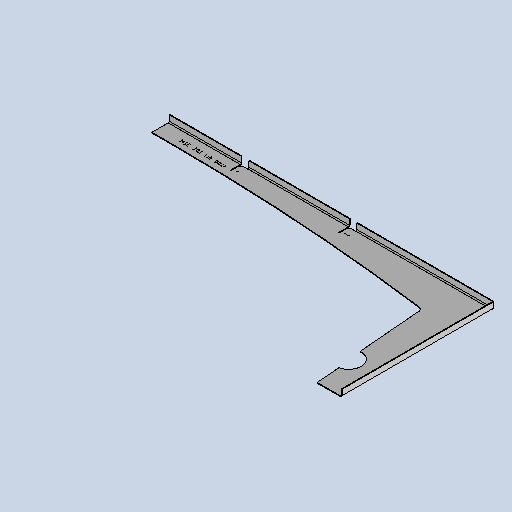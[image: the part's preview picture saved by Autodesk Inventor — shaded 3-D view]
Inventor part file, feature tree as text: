
AUTODESK INVENTOR PART (.ipt)
format: ipt  version: 2025 (Build 290162010, 162A)  size: 378,880 bytes
history: native  units: mm
features: other x6, sheet_metal_op x4, sketch x4, extrude x1
ambient origin geometry x8: Origin, YZ Plane, XZ Plane, XY Plane, X Axis, Y Axis, Z Axis, Center Point
bodies: Solid1 (feature_tree)
feature tree (15):
  sheet_metal_op  "Face1"
  other  "Mark3"
  sheet_metal_op  "Flange1"
  extrude  "Extrusion3"  Depth=2.0mm
  other  "Corner Chamfer2"
  other  "A-Side Definition"
  sketch  "Sketch1"  dims[d3=40.0mm d5=2.0mm]
  other  "Plate1"
  sketch  "Sketch2"  dims[d25=6.0mm d27=3.0mm d31=3.0mm]
  other  "Plate2"
  sheet_metal_op  "Bend1"
  sheet_metal_op  "Corner1"
  sketch  "Sketch7"  dims[d37=2.0mm]
  sketch  "Sketch8"  dims[d38=1.0mm d39=4.0mm d40=2.75mm d41=20.0mm d42=90.0deg d43=2.75mm d44=8.0mm d45=0.5mm d46=2.75mm d52=31.0mm d53=50.0mm d57=32.0mm d66=67.869053mm d76=51.965032mm d90=1500.0mm d92=2100.0mm d93=8.0mm d94=50.0mm d95=50.0mm d96=3.0mm d97=10.0mm d102=3.0mm d104=5.0mm d105=70.0mm d135=20.0mm d136=12.0mm d137=12.0mm d138=150.0mm d139=300.0mm d140=2.1mm d141=21.0mm d142=21.0mm d143=300.0mm d144=31.0mm d146=30.0mm d147=2.0mm d148=20.0mm d150=5.0mm d151=0.0mm d152=0.0mm d156=150.0mm d157=6.0mm d158=6.0mm d159=45.0deg d160=67.948864mm d161=51.991501mm d162=4.0mm d164=50.0mm d165=222.0mm d166=16.545721mm d167=900.0mm]
  other  "Definition1"
